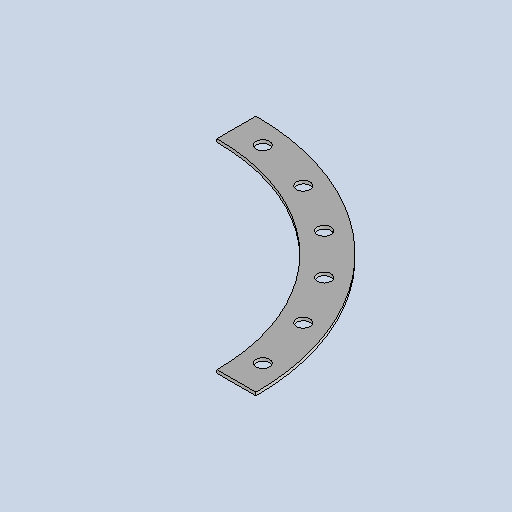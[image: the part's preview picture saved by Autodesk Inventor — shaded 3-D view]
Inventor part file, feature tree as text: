
AUTODESK INVENTOR PART (.ipt)
format: ipt  version: 2025 (Build 290162010, 162A)  size: 152,576 bytes
history: native  units: mm
features: sketch x2, other x2, sheet_metal_op x1, extrude x1, pattern_circular x1
ambient origin geometry x8: Origin, YZ Plane, XZ Plane, XY Plane, X Axis, Y Axis, Z Axis, Center Point
bodies: Solid1 (feature_tree)
feature tree (7):
  sheet_metal_op  "Face1"
  extrude  "Extrusion2"  Depth=600.0mm
  pattern_circular  "Circular Pattern1"  Count=64  [1 undecoded]
  sketch  "Sketch1"  dims[d0=502.0mm d1=600.0mm d2=640.0mm]
  other  "Plate1"
  sketch  "Sketch3"  dims[d5=4.0mm d12=550.0mm d13=1.308997mm d14=17.0mm d15=0.0mm d16=0.0mm d17=60.0mm d18=75.0deg]
  other  "Definition1"
note: 1 required parameter value undecoded (feature->parameter linkage not recoverable at this tier; creation-order binding heuristic only, values carry confidence <= 0.55)
